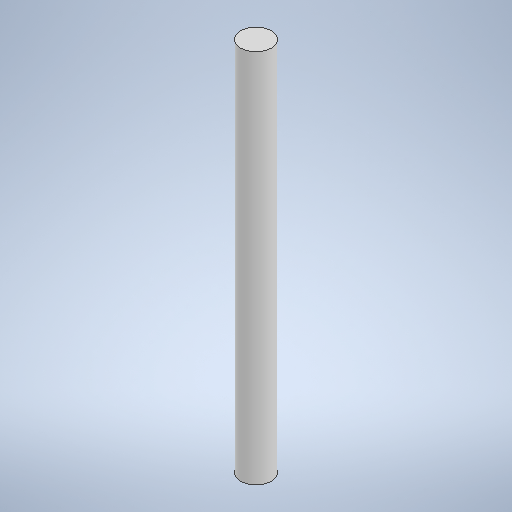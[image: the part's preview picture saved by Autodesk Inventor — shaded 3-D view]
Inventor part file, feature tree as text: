
AUTODESK INVENTOR PART (.ipt)
format: ipt  version: 2025.2 (Build 292293000, 293)  size: 244,736 bytes
history: native  units: mm
features: extrude x1, sketch x1
ambient origin geometry x8: Origin, YZ Plane, XZ Plane, XY Plane, X Axis, Y Axis, Z Axis, Center Point
bodies: Solid1 (feature_tree)
feature tree (2):
  extrude  "Extrusion1"  Depth=78.0mm TaperAngle=0.0deg
  sketch  "Sketch1"  dims[d0=6.35mm d1=78.0mm d2=0.0mm]
